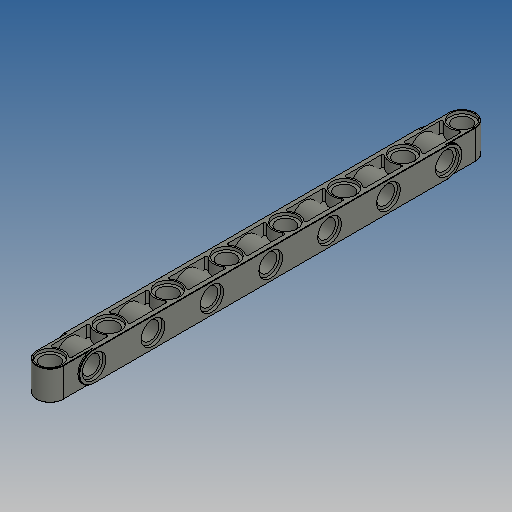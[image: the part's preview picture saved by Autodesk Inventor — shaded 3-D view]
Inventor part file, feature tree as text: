
AUTODESK INVENTOR PART (.ipt)
format: ipt  version: 2025 (Build 290162010, 162A)  size: 512,000 bytes
history: native  units: mm
features: sketch x8, extrude x7, mirror x3, fillet x2, delete_face x1, hole x1, pattern_linear x1
ambient origin geometry x8: Origin, YZ Plane, XZ Plane, XY Plane, X Axis, Y Axis, Z Axis, Center Point
bodies: Solid1 (feature_tree)
feature tree (23):
  extrude  "Extrusion1"  Depth=7.2mm
  sketch  "Sketch6"  dims[d48=112.0mm d49=6.4mm d50=4.8mm]
  extrude  "Extrusion7"  Depth=0.8mm TaperAngle=0.0deg
  extrude  "Extrusion8"  Depth=6.4mm
  mirror  "Mirror1"
  fillet  "Fillet2"  Radius=4.8mm
  mirror  "Spiegeln2"
  extrude  "Extrusion9"  Depth=0.8mm
  delete_face  "Fläche löschen1"
  fillet  "Rundung3"  Radius=70.0mm
  mirror  "Spiegeln3"
  extrude  "Extrusion10"  Depth=0.1mm
  extrude  "Extrusion11"  Depth=0.1mm
  extrude  "Extrusion12"  Depth=7.2mm TaperAngle=0.0deg
  hole  "Bohrung1"  [1 undecoded]
  pattern_linear  "Rechteckige Anordnung1"  Spacing1=0.0mm  [1 undecoded]
  sketch  "Sketch1"  dims[d14=8.0mm d15=0.0mm d32=7.2mm]
  sketch  "Skizze - Rechteckige Anordnung1"  dims[d41=0.8mm d42=0.0mm d43=3.1mm d44=0.0mm]
  sketch  "Skizze9"  dims[d51=16.0mm d52=0.8mm d53=70.0mm]
  sketch  "Skizze10"  dims[d55=16.0mm d56=10.0mm d58=10.0mm d60=0.4mm d61=0.1mm]
  sketch  "Skizze11"  dims[d63=0.4mm d64=0.0mm d65=0.1mm]
  sketch  "Skizze12"  dims[d66=7.2mm d67=0.4mm d68=0.0mm]
  sketch  "Skizze13"  dims[d69=6.4mm d70=0.8mm d71=0.0mm d72=0.8mm d73=0.0mm d74=4.8mm d75=40.0mm d76=4.0mm d77=2.0mm d78=90.0deg d79=8.0mm d80=20.594885mm d81=70.0mm d83=16.0mm d62=0.5mm]
note: 2 required parameter values undecoded (feature->parameter linkage not recoverable at this tier; creation-order binding heuristic only, values carry confidence <= 0.55)
